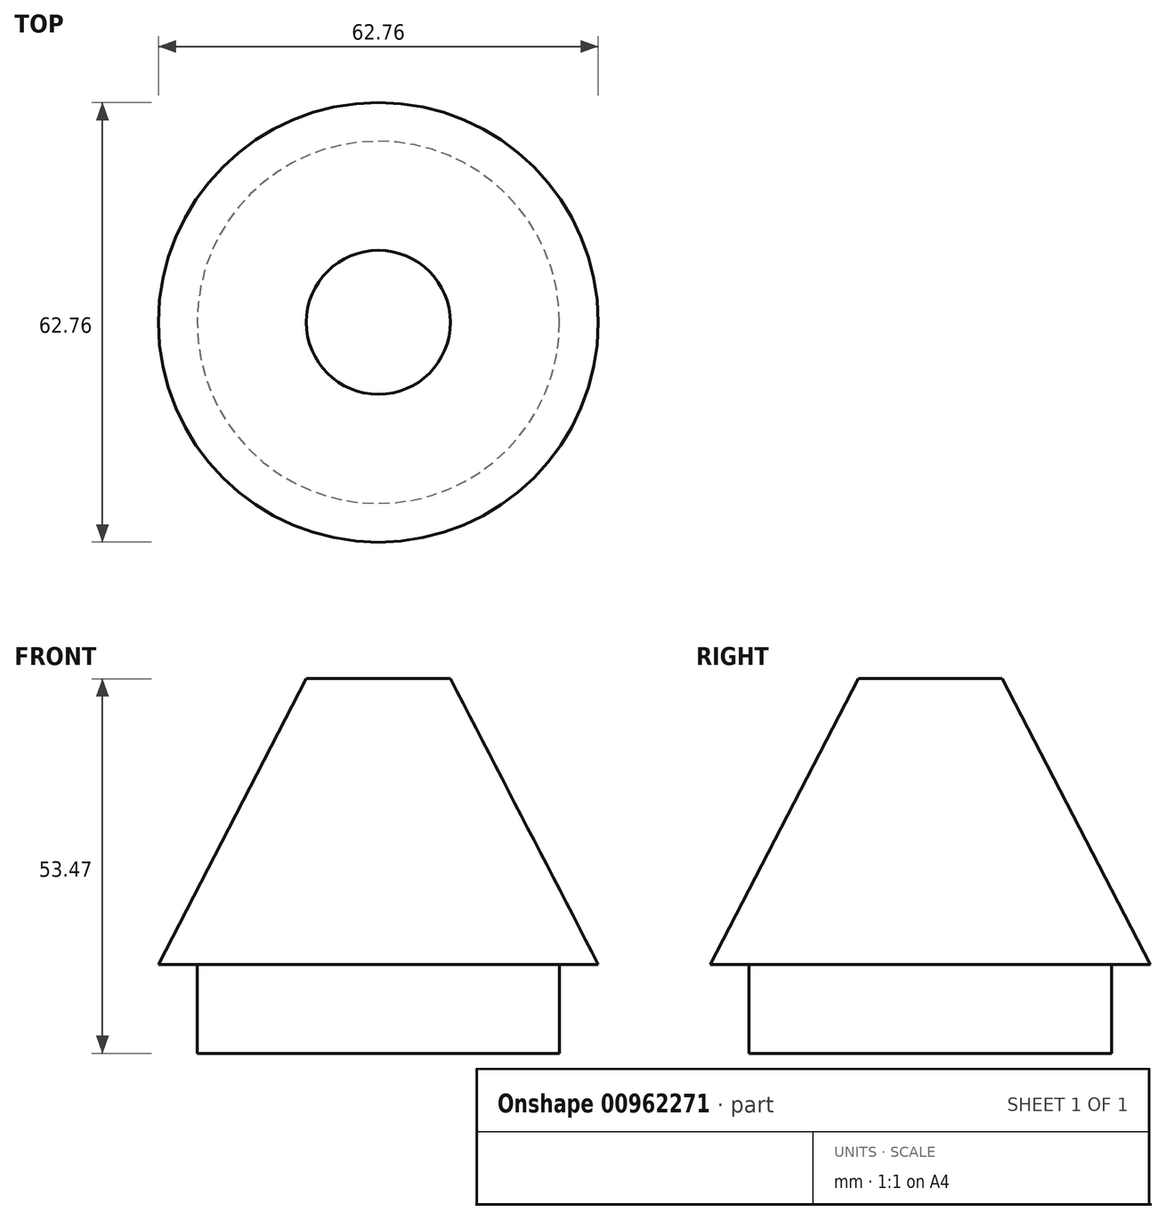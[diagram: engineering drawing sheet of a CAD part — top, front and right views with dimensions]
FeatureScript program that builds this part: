
annotation { "Feature Type Name" : "Feature", "Feature Type Description" : "" }
export const myFeature = defineFeature(function(context is Context, id is Id, definition is map)
    precondition{}
    {
        {
            var Q0;
            Q0=qCreatedBy(makeId("Front.planeOp"),FACE);
            var sketch = newSketch(context, id + "F0", { "sketchPlane" : qUnion([Q0])});
            skPoint(sketch, "E0", {"position": v(31.38, 0) * mm});
            skPoint(sketch, "E1", {"position": v(25.86, 0) * mm});
            skLineSegment(sketch, "E2.bottom", {"start": v(0, 0) * mm, "end": v(25.86, 0) * mm});
            skLineSegment(sketch, "E2.top", {"start": v(0, -12.7) * mm, "end": v(25.86, -12.7) * mm});
            skLineSegment(sketch, "E2.left", {"start": v(0, 0) * mm, "end": v(0, -12.7) * mm});
            skLineSegment(sketch, "E2.right", {"start": v(25.86, 0) * mm, "end": v(25.86, -12.7) * mm});
            skLineSegment(sketch, "E3", {"start": v(21.1, 0) * mm, "end": v(0, 40.77) * mm});
            skLineSegment(sketch, "E4", {"start": v(31.38, 0) * mm, "end": v(10.28, 40.77) * mm});
            skLineSegment(sketch, "E5", {"start": v(0, 40.77) * mm, "end": v(10.28, 40.77) * mm});
            skLineSegment(sketch, "E6", {"start": v(25.86, 0) * mm, "end": v(31.38, 0) * mm});
            skLineSegment(sketch, "E7", {"start": v(0, 62.86) * mm, "end": v(0, -38.7) * mm});
            skLineSegment(sketch, "E8", {"start": v(21.1, 0) * mm, "end": v(25.86, 0) * mm});
            skLineSegment(sketch, "E9", {"start": v(0, 0) * mm, "end": v(21.1, 0) * mm});
            skSolve(sketch);
        }
        {
            var Q0;
            {var subQ0=sQuery(id+"F0.wireOp",EDGE,"E3");Q0=makeQuery(id+"F0.imprint","IMPRINT",FACE,{"disambiguationData":[TD([[makeQuery(id+"F0.imprint","IMPRINT",EDGE,{"derivedFrom":subQ0}),1.0]])]});}
            var Q1;
            Q1=makeQuery(id+"F0.imprint","IMPRINT",FACE,{"disambiguationData":[TD([[makeQuery(id+"F0.imprint","IMPRINT",EDGE,{"derivedFrom":sQuery(id+"F0.wireOp",EDGE,"E3")}),-1.0]])]});
            var Q2;
            {var subQ1=sQuery(id+"F0.wireOp",EDGE,"E2.top");Q2=makeQuery(id+"F0.imprint","IMPRINT",FACE,{"disambiguationData":[TD([[makeQuery(id+"F0.imprint","IMPRINT",EDGE,{"derivedFrom":subQ1}),1.0]])]});}
            var Q3;
            Q3=sQuery(id+"F0.wireOp",EDGE,"E7");
            revolve(context, id + "F1", {"surfaceOperationType" : NewSurfaceOperationType.NEW, "entities" : qUnion([Q0, Q1, Q2]), "axis" : qUnion([Q3]), "revolveType" : RevolveType.FULL});
        }
    });
